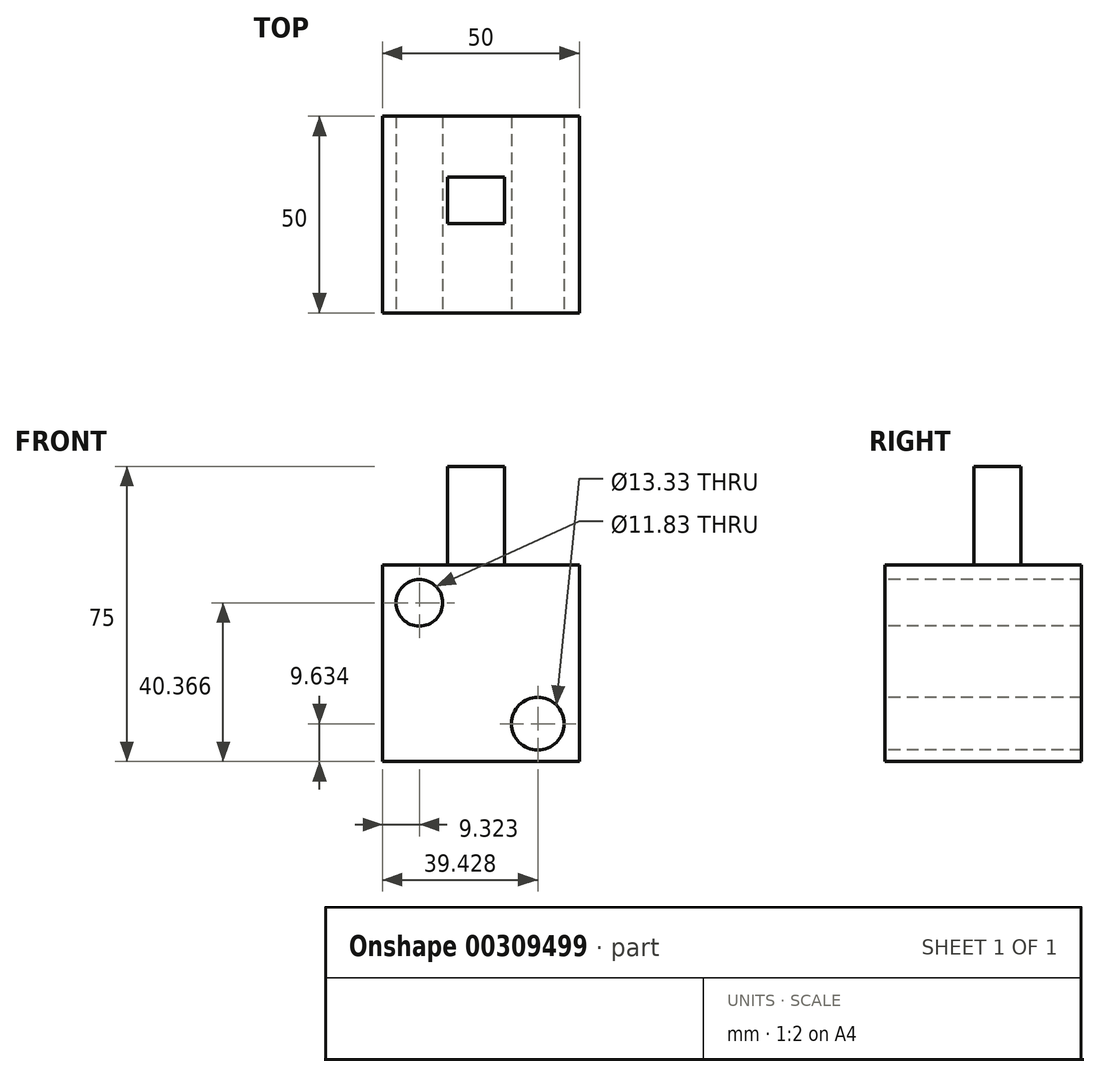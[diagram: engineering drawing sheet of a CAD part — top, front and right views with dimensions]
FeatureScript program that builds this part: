
annotation { "Feature Type Name" : "Feature", "Feature Type Description" : "" }
export const myFeature = defineFeature(function(context is Context, id is Id, definition is map)
    precondition{}
    {
        {
            var Q0;
            Q0=qCreatedBy(makeId("Top.planeOp"),FACE);
            var sketch = newSketch(context, id + "F0", { "sketchPlane" : qUnion([Q0])});
            skLineSegment(sketch, "E0.bottom", {"start": v(-31, 27.3) * mm, "end": v(19, 27.3) * mm});
            skLineSegment(sketch, "E0.top", {"start": v(-31, -22.7) * mm, "end": v(19, -22.7) * mm});
            skLineSegment(sketch, "E0.left", {"start": v(-31, 27.3) * mm, "end": v(-31, -22.7) * mm});
            skLineSegment(sketch, "E0.right", {"start": v(19, 27.3) * mm, "end": v(19, -22.7) * mm});
            skSolve(sketch);
        }
        {
            var Q0;
            Q0=makeQuery(id+"F0.imprint","IMPRINT",FACE,{"disambiguationData":[TD([[makeQuery(id+"F0.imprint","IMPRINT",EDGE,{"derivedFrom":sQuery(id+"F0.wireOp",EDGE,"E0.bottom")}),-1.0]])]});
            extrude(context, id + "F1", {"entities" : qUnion([Q0]), "depth" : 50 * mm});
        }
        {
            var Q0;
            Q0=makeQuery(id+"F1.opExtrude","SWEPT_FACE",FACE,{"disambiguationData":[OSD([sQuery(id+"F0.wireOp",EDGE,"E0.top")])]});
            var sketch = newSketch(context, id + "F2", { "sketchPlane" : qUnion([Q0])});
            skCircle(sketch, "E1", {"center": v(-21.68, 40.37) * mm, "radius": 5.92 * mm});
            skCircle(sketch, "E2", {"center": v(8.43, 9.63) * mm, "radius": 6.67 * mm});
            skSolve(sketch);
        }
        {
            var Q0;
            Q0=makeQuery(id+"F2.imprint","IMPRINT",FACE,{"disambiguationData":[TD([[makeQuery(id+"F2.imprint","IMPRINT",EDGE,{"derivedFrom":sQuery(id+"F2.wireOp",EDGE,"E1")}),1.0]])]});
            var Q1;
            Q1=makeQuery(id+"F2.imprint","IMPRINT",FACE,{"disambiguationData":[TD([[makeQuery(id+"F2.imprint","IMPRINT",EDGE,{"derivedFrom":sQuery(id+"F2.wireOp",EDGE,"E2")}),1.0]])]});
            extrude(context, id + "F3", {"entities" : qUnion([Q0, Q1]), "operationType" : NewBodyOperationType.REMOVE, "endBound" : BoundingType.THROUGH_ALL, "oppositeDirection" : true, "depth" : 25 * mm});
        }
        {
            var Q0;
            Q0=makeQuery(id+"F1.opExtrude","CAP_FACE",FACE,{"disambiguationData":[OSD([sQuery(id+"F0.wireOp",EDGE,"E0.bottom"),sQuery(id+"F0.wireOp",EDGE,"E0.top"),sQuery(id+"F0.wireOp",EDGE,"E0.left"),sQuery(id+"F0.wireOp",EDGE,"E0.right")])],"isStart":false});
            var sketch = newSketch(context, id + "F4", { "sketchPlane" : qUnion([Q0])});
            skLineSegment(sketch, "E3.bottom", {"start": v(-14.46, 11.87) * mm, "end": v(0, 11.87) * mm});
            skLineSegment(sketch, "E3.top", {"start": v(-14.46, 0) * mm, "end": v(0, 0) * mm});
            skLineSegment(sketch, "E3.left", {"start": v(-14.46, 11.87) * mm, "end": v(-14.46, 0) * mm});
            skLineSegment(sketch, "E3.right", {"start": v(0, 11.87) * mm, "end": v(0, 0) * mm});
            skSolve(sketch);
        }
        {
            var Q0;
            Q0 = qSketchRegion(id + "F4", true);
            extrude(context, id + "F5", {"entities" : qUnion([Q0]), "operationType" : NewBodyOperationType.ADD, "depth" : 25 * mm});
        }
    });
